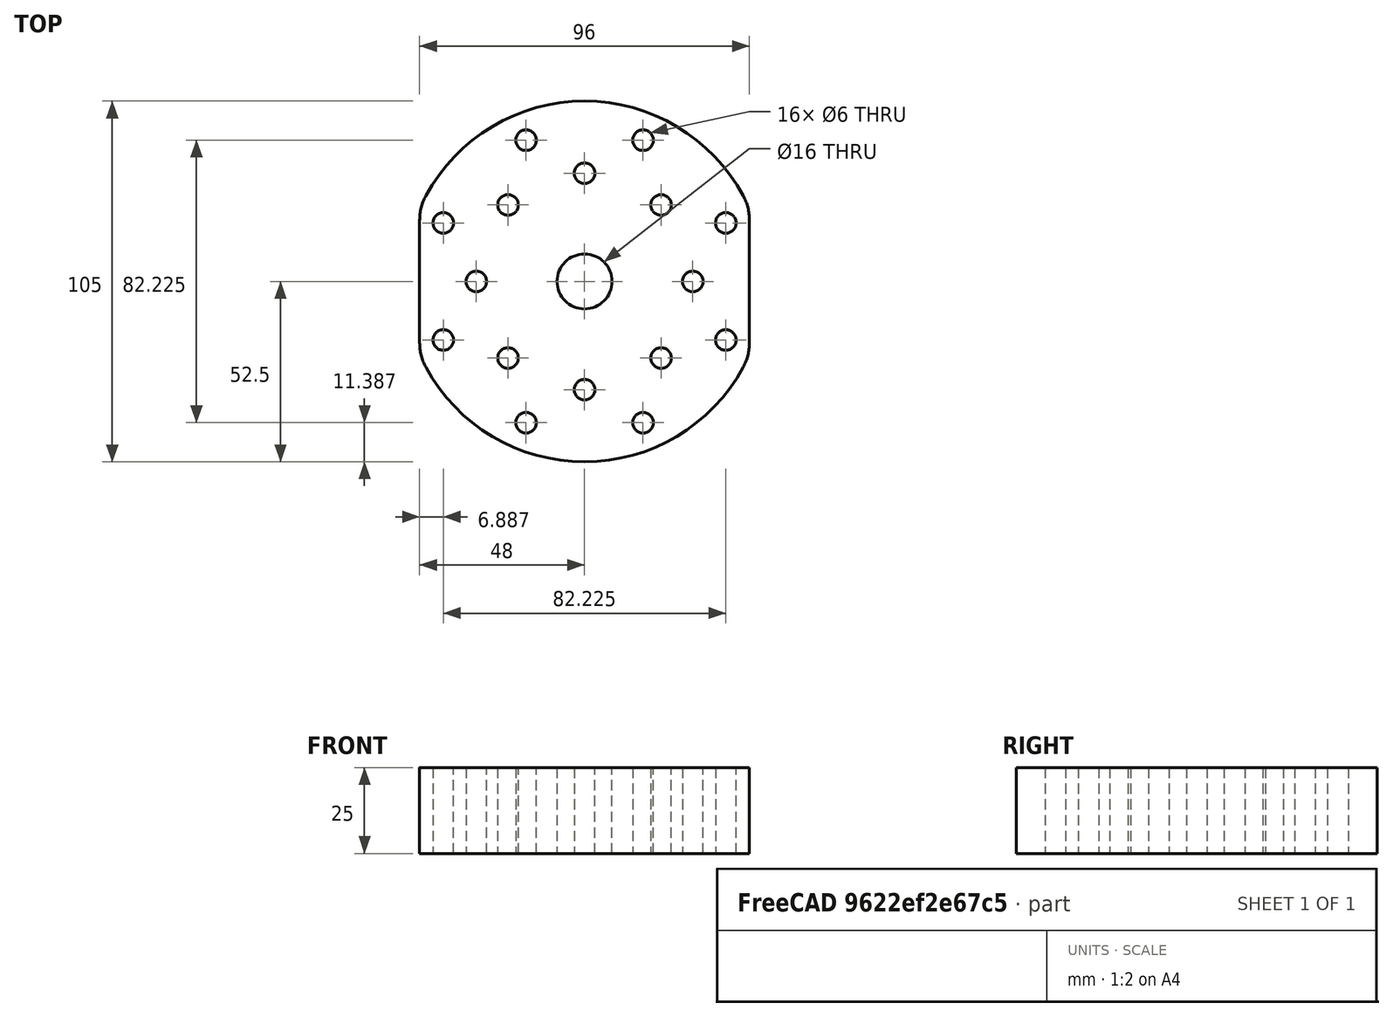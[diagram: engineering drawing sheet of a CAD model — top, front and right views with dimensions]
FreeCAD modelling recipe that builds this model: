
FCSTD DOCUMENT  (FreeCAD 0.19R24267 +99 (Git))
Label: V2 Load cell DYLF-102 mounting plate
License: All rights reserved
LicenseURL: http://en.wikipedia.org/wiki/All_rights_reserved
objects: Sketcher::SketchObject×1, PartDesign::Pad×1, PartDesign::Body×1
note: 4 computed .brp shape members not serialized (recipe doc carries the construction recipe); baked Part::Feature solids carry a one-line shape summary decoded from their .brp

FEATURE [Sketcher::SketchObject] Sketch
  FullyConstrained = true
  MapMode = 5
  Support = -> [XY_Plane]
  sketch-geometry (80):
    g0: Circle CenterX=0 CenterY=0 CenterZ=0 NormalX=0 NormalY=0 NormalZ=1 AngleXU=0 Radius=44.5
    g1: ArcOfCircle CenterX=0 CenterY=0 CenterZ=0 NormalX=0 NormalY=0 NormalZ=1 AngleXU=0 Radius=52.5 StartAngle=3.63653 EndAngle=5.78825
    g2: Circle CenterX=0 CenterY=0 CenterZ=0 NormalX=0 NormalY=0 NormalZ=1 AngleXU=0 Radius=31.5
    g3: Circle CenterX=0 CenterY=0 CenterZ=0 NormalX=0 NormalY=0 NormalZ=1 AngleXU=0 Radius=3
    g4: Circle CenterX=22.2739 CenterY=22.2739 CenterZ=0 NormalX=0 NormalY=0 NormalZ=1 AngleXU=0 Radius=3
    g5: Circle CenterX=0 CenterY=31.5 CenterZ=0 NormalX=0 NormalY=0 NormalZ=1 AngleXU=0 Radius=3
    g6: Circle CenterX=31.5 CenterY=0 CenterZ=0 NormalX=0 NormalY=0 NormalZ=1 AngleXU=0 Radius=3
    g7: Circle CenterX=0 CenterY=-31.5 CenterZ=0 NormalX=0 NormalY=0 NormalZ=1 AngleXU=0 Radius=3
    g8: Circle CenterX=-22.2739 CenterY=-22.2739 CenterZ=0 NormalX=0 NormalY=0 NormalZ=1 AngleXU=0 Radius=3
    g9: Circle CenterX=-31.5 CenterY=0 CenterZ=0 NormalX=0 NormalY=0 NormalZ=1 AngleXU=0 Radius=3
    g10: Circle CenterX=-22.2739 CenterY=22.2739 CenterZ=0 NormalX=0 NormalY=0 NormalZ=1 AngleXU=0 Radius=3
    g11: Circle CenterX=22.2739 CenterY=-22.2739 CenterZ=0 NormalX=0 NormalY=0 NormalZ=1 AngleXU=0 Radius=3
    g12: LineSegment StartX=-22.2739 StartY=22.2739 StartZ=0 EndX=22.2739 EndY=-22.2739 EndZ=0
    g13: LineSegment StartX=-22.2739 StartY=-22.2739 StartZ=0 EndX=22.2739 EndY=22.2739 EndZ=0
    g14: Circle CenterX=-17.0294 CenterY=41.1126 CenterZ=0 NormalX=0 NormalY=0 NormalZ=1 AngleXU=0 Radius=3
    g15: Circle CenterX=17.0294 CenterY=41.1126 CenterZ=0 NormalX=0 NormalY=0 NormalZ=1 AngleXU=0 Radius=3
    g16: Circle CenterX=41.1126 CenterY=17.0294 CenterZ=0 NormalX=0 NormalY=0 NormalZ=1 AngleXU=0 Radius=3
    g17: Circle CenterX=41.1126 CenterY=-17.0294 CenterZ=0 NormalX=0 NormalY=0 NormalZ=1 AngleXU=0 Radius=3
    g18: Circle CenterX=17.0294 CenterY=-41.1126 CenterZ=0 NormalX=0 NormalY=0 NormalZ=1 AngleXU=0 Radius=3
    g19: Circle CenterX=-17.0294 CenterY=-41.1126 CenterZ=0 NormalX=0 NormalY=0 NormalZ=1 AngleXU=0 Radius=3
    g20: Circle CenterX=-41.1126 CenterY=-17.0294 CenterZ=0 NormalX=0 NormalY=0 NormalZ=1 AngleXU=0 Radius=3
    g21: Circle CenterX=-41.1126 CenterY=17.0294 CenterZ=0 NormalX=0 NormalY=0 NormalZ=1 AngleXU=0 Radius=3
    g22: LineSegment StartX=-31.5 StartY=0 StartZ=0 EndX=-41.1126 EndY=17.0294 EndZ=0
    g23: LineSegment StartX=-41.1126 StartY=17.0294 StartZ=0 EndX=-22.2739 EndY=22.2739 EndZ=0
    g24: LineSegment StartX=-22.2739 StartY=22.2739 StartZ=0 EndX=-17.0294 EndY=41.1126 EndZ=0
    g25: LineSegment StartX=-17.0294 StartY=41.1126 StartZ=0 EndX=0 EndY=31.5 EndZ=0
    g26: LineSegment StartX=0 StartY=31.5 StartZ=0 EndX=17.0294 EndY=41.1126 EndZ=0
    g27: LineSegment StartX=17.0294 StartY=41.1126 StartZ=0 EndX=22.2739 EndY=22.2739 EndZ=0
    g28: LineSegment StartX=22.2739 StartY=22.2739 StartZ=0 EndX=41.1126 EndY=17.0294 EndZ=0
    g29: LineSegment StartX=41.1126 StartY=17.0294 StartZ=0 EndX=31.5 EndY=0 EndZ=0
    g30: LineSegment StartX=31.5 StartY=0 StartZ=0 EndX=41.1126 EndY=-17.0294 EndZ=0
    g31: LineSegment StartX=41.1126 StartY=-17.0294 StartZ=0 EndX=22.2739 EndY=-22.2739 EndZ=0
    g32: LineSegment StartX=22.2739 StartY=-22.2739 StartZ=0 EndX=17.0294 EndY=-41.1126 EndZ=0
    g33: LineSegment StartX=17.0294 StartY=-41.1126 StartZ=0 EndX=0 EndY=-31.5 EndZ=0
    g34: LineSegment StartX=0 StartY=-31.5 StartZ=0 EndX=-17.0294 EndY=-41.1126 EndZ=0
    g35: LineSegment StartX=-17.0294 StartY=-41.1126 StartZ=0 EndX=-22.2739 EndY=-22.2739 EndZ=0
    g36: LineSegment StartX=-22.2739 StartY=-22.2739 StartZ=0 EndX=-41.1126 EndY=-17.0294 EndZ=0
    g37: LineSegment StartX=-41.1126 StartY=-17.0294 StartZ=0 EndX=-31.5 EndY=0 EndZ=0
    g38: LineSegment StartX=-48 StartY=17.8115 StartZ=0 EndX=-48 EndY=-17.8115 EndZ=0
    g39: LineSegment StartX=48 StartY=17.8115 StartZ=0 EndX=48 EndY=-17.8115 EndZ=0
    g40: ArcOfCircle CenterX=0 CenterY=0 CenterZ=0 NormalX=0 NormalY=0 NormalZ=1 AngleXU=0 Radius=52.5 StartAngle=0.494934 EndAngle=2.64666
    g41: ArcOfCircle CenterX=-33 CenterY=-17.8115 CenterZ=0 NormalX=0 NormalY=0 NormalZ=1 AngleXU=0 Radius=15 StartAngle=3.14159 EndAngle=3.63653
    g42: ArcOfCircle CenterX=-33 CenterY=17.8115 CenterZ=0 NormalX=0 NormalY=0 NormalZ=1 AngleXU=0 Radius=15 StartAngle=2.64666 EndAngle=3.14159
    g43: ArcOfCircle CenterX=33 CenterY=17.8115 CenterZ=0 NormalX=0 NormalY=0 NormalZ=1 AngleXU=0 Radius=15 StartAngle=0 EndAngle=0.494934
    g44: ArcOfCircle CenterX=33 CenterY=-17.8115 CenterZ=0 NormalX=0 NormalY=0 NormalZ=1 AngleXU=0 Radius=15 StartAngle=5.78825 EndAngle=6.28319
    g45: LineSegment StartX=-17.0294 StartY=44.1126 StartZ=0 EndX=-17.0294 EndY=38.1126 EndZ=0
    g46: LineSegment StartX=-20.0294 StartY=41.1126 StartZ=0 EndX=-14.0294 EndY=41.1126 EndZ=0
    g47: LineSegment StartX=-3 StartY=31.5 StartZ=0 EndX=3 EndY=31.5 EndZ=0
    g48: LineSegment StartX=0 StartY=34.5 StartZ=0 EndX=0 EndY=28.5 EndZ=0
    g49: LineSegment StartX=17.0294 StartY=44.1126 StartZ=0 EndX=17.0294 EndY=38.1126 EndZ=0
    g50: LineSegment StartX=14.0294 StartY=41.1126 StartZ=0 EndX=20.0294 EndY=41.1126 EndZ=0
    g51: LineSegment StartX=19.2739 StartY=22.2739 StartZ=0 EndX=25.2739 EndY=22.2739 EndZ=0
    g52: LineSegment StartX=22.2739 StartY=25.2739 StartZ=0 EndX=22.2739 EndY=19.2739 EndZ=0
    g53: LineSegment StartX=41.1126 StartY=20.0294 StartZ=0 EndX=41.1126 EndY=14.0294 EndZ=0
    g54: LineSegment StartX=38.1126 StartY=17.0294 StartZ=0 EndX=44.1126 EndY=17.0294 EndZ=0
    g55: LineSegment StartX=28.5 StartY=0 StartZ=0 EndX=34.5 EndY=0 EndZ=0
    g56: LineSegment StartX=31.5 StartY=-3 StartZ=0 EndX=31.5 EndY=3 EndZ=0
    g57: LineSegment StartX=41.1126 StartY=-14.0294 StartZ=0 EndX=41.1126 EndY=-20.0294 EndZ=0
    g58: LineSegment StartX=38.1126 StartY=-17.0294 StartZ=0 EndX=44.1126 EndY=-17.0294 EndZ=0
    g59: LineSegment StartX=22.2739 StartY=-19.2739 StartZ=0 EndX=22.2739 EndY=-25.2739 EndZ=0
    g60: LineSegment StartX=19.2739 StartY=-22.2739 StartZ=0 EndX=25.2739 EndY=-22.2739 EndZ=0
    g61: LineSegment StartX=14.0294 StartY=-41.1126 StartZ=0 EndX=20.0294 EndY=-41.1126 EndZ=0
    g62: LineSegment StartX=17.0294 StartY=-38.1126 StartZ=0 EndX=17.0294 EndY=-44.1126 EndZ=0
    g63: LineSegment StartX=-3 StartY=-31.5 StartZ=0 EndX=3 EndY=-31.5 EndZ=0
    g64: LineSegment StartX=0 StartY=-28.5 StartZ=0 EndX=0 EndY=-34.5 EndZ=0
    g65: LineSegment StartX=-17.0294 StartY=-38.1126 StartZ=0 EndX=-17.0294 EndY=-44.1126 EndZ=0
    g66: LineSegment StartX=-20.0294 StartY=-41.1126 StartZ=0 EndX=-14.0294 EndY=-41.1126 EndZ=0
    g67: LineSegment StartX=-25.2739 StartY=-22.2739 StartZ=0 EndX=-19.2739 EndY=-22.2739 EndZ=0
    g68: LineSegment StartX=-22.2739 StartY=-19.2739 StartZ=0 EndX=-22.2739 EndY=-25.2739 EndZ=0
    g69: LineSegment StartX=-44.1126 StartY=-17.0294 StartZ=0 EndX=-38.1126 EndY=-17.0294 EndZ=0
    g70: LineSegment StartX=-41.1126 StartY=-14.0294 StartZ=0 EndX=-41.1126 EndY=-20.0294 EndZ=0
    g71: LineSegment StartX=-34.5 StartY=0 StartZ=0 EndX=-28.5 EndY=0 EndZ=0
    g72: LineSegment StartX=-31.5 StartY=3 StartZ=0 EndX=-31.5 EndY=-3 EndZ=0
    g73: LineSegment StartX=-41.1126 StartY=20.0294 StartZ=0 EndX=-41.1126 EndY=14.0294 EndZ=0
    g74: LineSegment StartX=-44.1126 StartY=17.0294 StartZ=0 EndX=-38.1126 EndY=17.0294 EndZ=0
    g75: LineSegment StartX=-25.2739 StartY=22.2739 StartZ=0 EndX=-19.2739 EndY=22.2739 EndZ=0
    g76: LineSegment StartX=-22.2739 StartY=25.2739 StartZ=0 EndX=-22.2739 EndY=19.2739 EndZ=0
    g77: LineSegment StartX=0 StartY=3 StartZ=0 EndX=0 EndY=-3 EndZ=0
    g78: LineSegment StartX=-3 StartY=0 StartZ=0 EndX=3 EndY=0 EndZ=0
    g79: Circle CenterX=0 CenterY=0 CenterZ=0 NormalX=0 NormalY=0 NormalZ=1 AngleXU=0 Radius=8
  constraints (247):
    c: Coincident(g0,g-1)
    c: Coincident(g1,g0)
    c: Coincident(g2,g0)
    c: Coincident(g3,g0)
    c: PointOnObject(g4,g2)
    c: PointOnObject(g5,g2)
    c: PointOnObject(g6,g2)
    c: PointOnObject(g7,g2)
    c: PointOnObject(g8,g2)
    c: PointOnObject(g9,g2)
    c: PointOnObject(g10,g2)
    c: PointOnObject(g5,g-2)
    c: PointOnObject(g6,g-1)
    c: PointOnObject(g9,g-1)
    c: PointOnObject(g7,g-2)
    c: PointOnObject(g11,g2)
    c: Coincident(g12,g10)
    c: Coincident(g12,g11)
    c: Coincident(g13,g8)
    c: Coincident(g13,g4)
    c: PointOnObject(g0,g12)
    c: PointOnObject(g0,g13)
    c: Angle(g-1,g13) = 0.785398
    c: Angle(g-1,g12) = 2.35619
    c: Equal(g9,g10)
    c: Equal(g10,g5)
    c: Equal(g5,g4)
    c: Equal(g4,g6)
    c: Equal(g6,g11)
    c: Equal(g11,g7)
    c: Equal(g7,g8)
    c: PointOnObject(g14,g0)
    c: PointOnObject(g15,g0)
    c: PointOnObject(g16,g0)
    c: PointOnObject(g17,g0)
    c: PointOnObject(g18,g0)
    c: PointOnObject(g19,g0)
    c: PointOnObject(g20,g0)
    c: PointOnObject(g21,g0)
    c: Coincident(g22,g9)
    c: Coincident(g22,g21)
    c: Coincident(g23,g21)
    c: Coincident(g23,g10)
    c: Coincident(g24,g10)
    c: Coincident(g24,g14)
    c: Coincident(g25,g14)
    c: Coincident(g25,g5)
    c: Coincident(g26,g5)
    c: Coincident(g26,g15)
    c: Coincident(g27,g15)
    c: Coincident(g27,g4)
    c: Coincident(g28,g4)
    c: Coincident(g28,g16)
    c: Coincident(g29,g16)
    c: Coincident(g29,g6)
    c: Coincident(g30,g6)
    c: Coincident(g30,g17)
    c: Coincident(g31,g17)
    c: Coincident(g31,g11)
    c: Coincident(g32,g11)
    c: Coincident(g32,g18)
    c: Coincident(g33,g18)
    c: Coincident(g33,g7)
    c: Coincident(g34,g7)
    c: Coincident(g34,g19)
    c: Coincident(g35,g19)
    c: Coincident(g35,g8)
    c: Coincident(g36,g8)
    c: Coincident(g36,g20)
    c: Coincident(g37,g20)
    c: Coincident(g37,g9)
    c: Equal(g15,g16)
    c: Equal(g16,g17)
    c: Equal(g17,g18)
    c: Equal(g19,g20)
    c: Equal(g23,g22)
    c: Equal(g22,g24)
    c: Equal(g25,g26)
    c: Equal(g27,g28)
    c: Equal(g29,g30)
    c: Equal(g31,g32)
    c: Equal(g33,g34)
    c: Equal(g35,g36)
    c: Coincident(g1,g40)
    c: Tangent(g1,g41) = -1.5708
    c: Tangent(g38,g41) = -1.5708
    c: Tangent(g40,g42) = -1.5708
    c: Tangent(g38,g42) = -1.5708
    c: Tangent(g39,g43) = 1.5708
    c: Tangent(g40,g43) = -1.5708
    c: Tangent(g1,g44) = -1.5708
    c: Tangent(g39,g44) = 1.5708
    c: Equal(g44,g41)
    c: Equal(g41,g42)
    c: Equal(g42,g43)
    c: Radius(g43) = 15
    c: Vertical(g39)
    c: DistanceX(g38,g39) = 96
    c: Equal(g38,g39)
    c: Symmetric(g38,g38,g-1)
    c: Equal(g3,g7)
    c: Equal(g7,g18)
    c: Equal(g8,g20)
    c: Equal(g10,g21)
    c: Equal(g21,g14)
    c: Diameter(g18) = 6
    c: PointOnObject(g45,g14)
    c: PointOnObject(g45,g14)
    c: Vertical(g45)
    c: PointOnObject(g46,g14)
    c: PointOnObject(g46,g14)
    c: Horizontal(g46)
    c: PointOnObject(g47,g5)
    c: PointOnObject(g47,g5)
    c: Horizontal(g47)
    c: PointOnObject(g48,g5)
    c: PointOnObject(g48,g5)
    c: PointOnObject(g49,g15)
    c: PointOnObject(g49,g15)
    c: Vertical(g49)
    c: PointOnObject(g50,g15)
    c: PointOnObject(g50,g15)
    c: Horizontal(g50)
    c: PointOnObject(g51,g4)
    c: PointOnObject(g51,g4)
    c: Horizontal(g51)
    c: PointOnObject(g52,g4)
    c: PointOnObject(g52,g4)
    c: Vertical(g52)
    c: PointOnObject(g53,g16)
    c: PointOnObject(g53,g16)
    c: Vertical(g53)
    c: PointOnObject(g54,g16)
    c: PointOnObject(g54,g16)
    c: Horizontal(g54)
    c: PointOnObject(g55,g6)
    c: PointOnObject(g55,g6)
    c: Horizontal(g55)
    c: PointOnObject(g56,g6)
    c: PointOnObject(g56,g6)
    c: PointOnObject(g57,g17)
    c: PointOnObject(g57,g17)
    c: Vertical(g57)
    c: PointOnObject(g58,g17)
    c: PointOnObject(g58,g17)
    c: Horizontal(g58)
    c: PointOnObject(g59,g11)
    c: PointOnObject(g59,g11)
    c: Vertical(g59)
    c: PointOnObject(g60,g11)
    c: PointOnObject(g60,g11)
    c: PointOnObject(g61,g18)
    c: PointOnObject(g61,g18)
    c: Horizontal(g61)
    c: PointOnObject(g62,g18)
    c: PointOnObject(g62,g18)
    c: Vertical(g62)
    c: PointOnObject(g63,g7)
    c: PointOnObject(g63,g7)
    c: Horizontal(g63)
    c: PointOnObject(g64,g7)
    c: PointOnObject(g64,g7)
    c: Vertical(g64)
    c: PointOnObject(g65,g19)
    c: PointOnObject(g65,g19)
    c: Vertical(g65)
    c: PointOnObject(g66,g19)
    c: PointOnObject(g66,g19)
    c: Horizontal(g66)
    c: PointOnObject(g67,g8)
    c: PointOnObject(g67,g8)
    c: Horizontal(g67)
    c: PointOnObject(g68,g8)
    c: PointOnObject(g68,g8)
    c: Vertical(g68)
    c: PointOnObject(g69,g20)
    c: PointOnObject(g69,g20)
    c: Horizontal(g69)
    c: PointOnObject(g70,g20)
    c: PointOnObject(g70,g20)
    c: Vertical(g70)
    c: PointOnObject(g71,g9)
    c: PointOnObject(g71,g9)
    c: Horizontal(g71)
    c: PointOnObject(g72,g9)
    c: PointOnObject(g72,g9)
    c: Vertical(g72)
    c: PointOnObject(g73,g21)
    c: PointOnObject(g73,g21)
    c: Vertical(g73)
    c: PointOnObject(g74,g21)
    c: PointOnObject(g74,g21)
    c: Horizontal(g74)
    c: PointOnObject(g75,g10)
    c: PointOnObject(g75,g10)
    c: Horizontal(g75)
    c: PointOnObject(g76,g10)
    c: PointOnObject(g76,g10)
    c: Vertical(g76)
    c: PointOnObject(g9,g71)
    c: PointOnObject(g9,g72)
    c: PointOnObject(g20,g70)
    c: PointOnObject(g20,g69)
    c: PointOnObject(g8,g68)
    c: PointOnObject(g8,g67)
    c: PointOnObject(g7,g63)
    c: PointOnObject(g7,g64)
    c: PointOnObject(g19,g66)
    c: PointOnObject(g19,g65)
    c: PointOnObject(g18,g62)
    c: PointOnObject(g18,g61)
    c: Horizontal(g60)
    c: PointOnObject(g11,g59)
    c: PointOnObject(g11,g60)
    c: PointOnObject(g17,g58)
    c: PointOnObject(g17,g57)
    c: Vertical(g56)
    c: PointOnObject(g6,g55)
    c: PointOnObject(g6,g56)
    c: PointOnObject(g16,g53)
    c: PointOnObject(g16,g54)
    c: PointOnObject(g4,g52)
    c: PointOnObject(g4,g51)
    c: PointOnObject(g15,g50)
    c: PointOnObject(g15,g49)
    c: Vertical(g48)
    c: PointOnObject(g5,g47)
    c: PointOnObject(g5,g48)
    c: PointOnObject(g14,g46)
    c: PointOnObject(g14,g45)
    c: PointOnObject(g10,g75)
    c: PointOnObject(g10,g76)
    c: PointOnObject(g21,g74)
    c: PointOnObject(g21,g73)
    c: Diameter(g2) = 63
    c: Diameter(g0) = 89
    c: Diameter(g1) = 105
    c: PointOnObject(g77,g3)
    c: PointOnObject(g77,g3)
    c: Vertical(g77)
    c: PointOnObject(g78,g3)
    c: PointOnObject(g78,g3)
    c: Horizontal(g78)
    c: PointOnObject(g1,g77)
    c: PointOnObject(g1,g78)
    c: Coincident(g79,g1)
    c: Diameter(g79) = 16
FEATURE [PartDesign::Pad] Pad
  Direction = (1,1,1)
  Length = 25
  Length2 = 100
  Profile = -> Sketch
  Type = 0
FEATURE [PartDesign::Body] Body
  Group = -> [Sketch,Pad]
  Origin = -> Origin
  Tip = -> Pad
